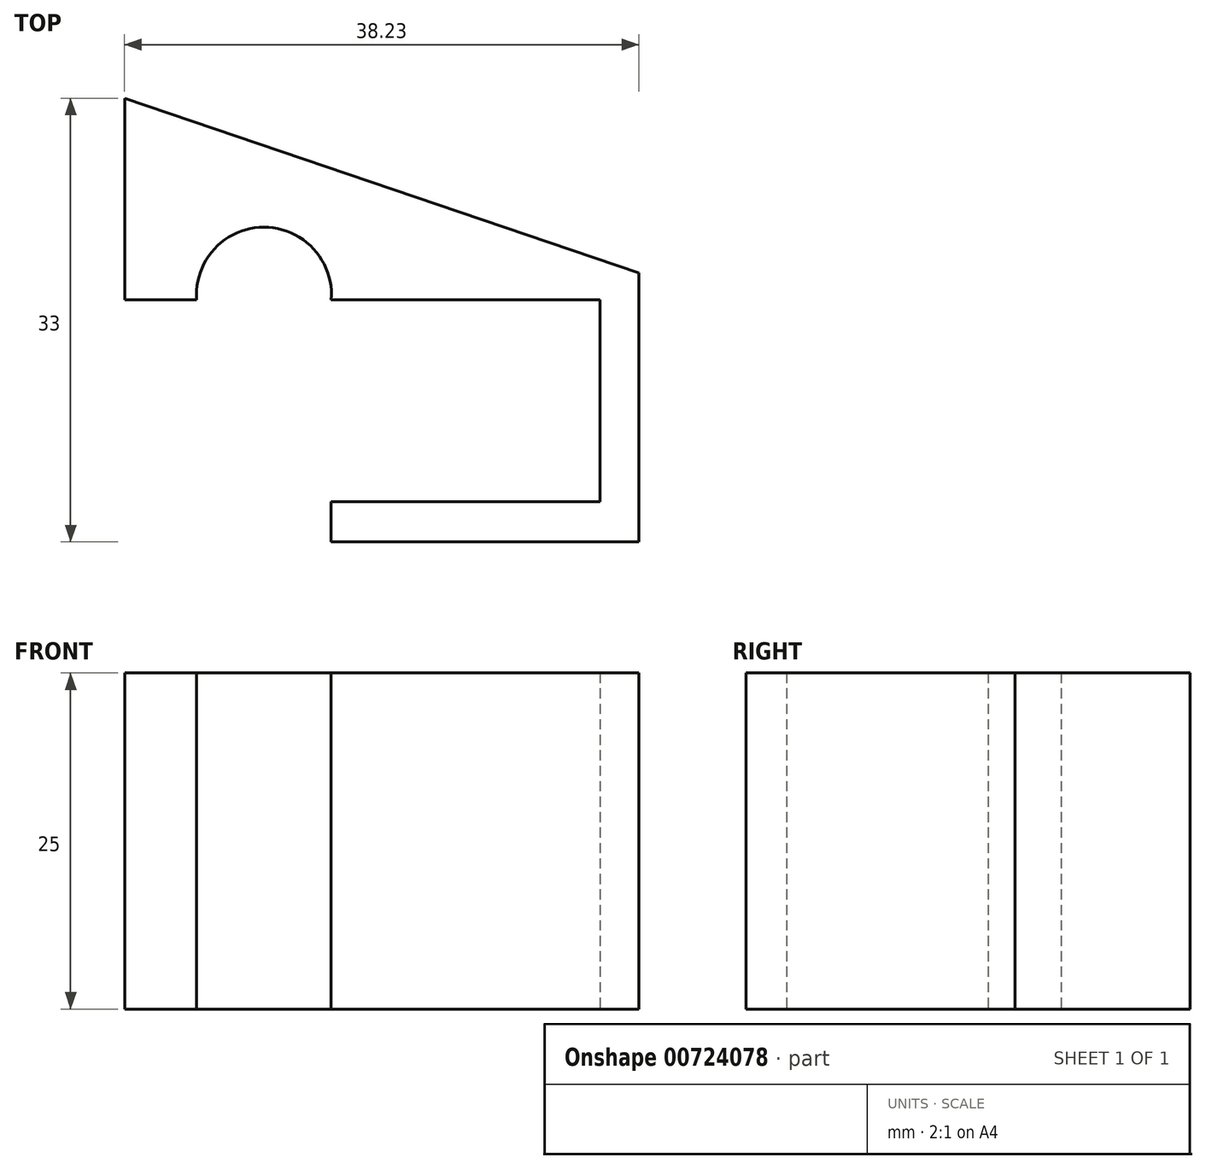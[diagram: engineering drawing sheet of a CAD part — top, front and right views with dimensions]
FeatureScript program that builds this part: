
annotation { "Feature Type Name" : "Feature", "Feature Type Description" : "" }
export const myFeature = defineFeature(function(context is Context, id is Id, definition is map)
    precondition{}
    {
        {
            var Q0;
            Q0=qCreatedBy(makeId("Top.planeOp"),FACE);
            var sketch = newSketch(context, id + "F0", { "sketchPlane" : qUnion([Q0])});
            skLineSegment(sketch, "E0", {"start": v(-39.83, -13.74) * mm, "end": v(-19.83, -13.74) * mm});
            skLineSegment(sketch, "E1", {"start": v(-49.83, -13.74) * mm, "end": v(-55.2, -13.74) * mm});
            skLineSegment(sketch, "E2", {"start": v(-19.83, -13.74) * mm, "end": v(-19.83, -28.74) * mm});
            skLineSegment(sketch, "E3", {"start": v(-19.83, -28.74) * mm, "end": v(-39.83, -28.74) * mm});
            skArc(sketch, "E4", {"start": v(-39.83, -13.74) * mm, "mid": v(-44.83, -8.33) * mm, "end": v(-49.83, -13.74) * mm});
            skLineSegment(sketch, "E5", {"start": v(-55.2, -13.74) * mm, "end": v(-55.2, 1.26) * mm});
            skLineSegment(sketch, "E6", {"start": v(-39.83, -28.74) * mm, "end": v(-39.83, -31.74) * mm});
            skLineSegment(sketch, "E7", {"start": v(-39.83, -31.74) * mm, "end": v(-19.97, -31.74) * mm});
            skLineSegment(sketch, "E8", {"start": v(-19.97, -31.74) * mm, "end": v(-16.97, -31.74) * mm});
            skLineSegment(sketch, "E9", {"start": v(-16.97, -31.74) * mm, "end": v(-16.97, -11.74) * mm});
            skLineSegment(sketch, "E10", {"start": v(-16.97, -11.74) * mm, "end": v(-55.2, 1.26) * mm});
            skSolve(sketch);
        }
        {
            var Q0;
            Q0=makeQuery(id+"F0.imprint","IMPRINT",FACE,{"disambiguationData":[TD([[makeQuery(id+"F0.imprint","IMPRINT",EDGE,{"derivedFrom":sQuery(id+"F0.wireOp",EDGE,"E0")}),1.0]])]});
            extrude(context, id + "F1", {"entities" : qUnion([Q0]), "depth" : 25 * mm, "offsetDistance" : 25 * mm});
        }
    });
